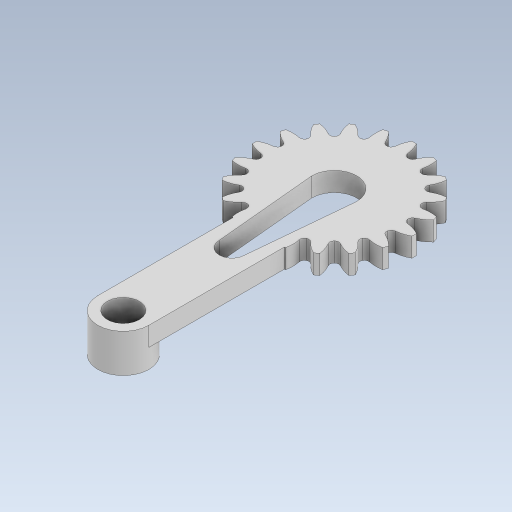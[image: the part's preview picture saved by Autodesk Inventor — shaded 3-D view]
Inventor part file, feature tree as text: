
AUTODESK INVENTOR PART (.ipt)
format: ipt  version: 2023.5 (Build 275446000, 446)  size: 549,888 bytes
history: native  units: in
note: dims shown in document units (in); Inventor stores cm internally (conversion verified against a paired STEP export)
features: extrude x5, sketch x3, fillet x1, pattern_circular x1, plane x1
ambient origin geometry x8: Origin, YZ Plane, XZ Plane, XY Plane, X Axis, Y Axis, Z Axis, Center Point
bodies: Solid1 (feature_tree)
feature tree (11):
  sketch  "Sketch1"  dims[d0=0.7874in d1=0.9843in]
  extrude  "Extrusion1"  Depth=0.9843in
  extrude  "Extrusion3"  Depth=0.0787in
  fillet  "Fillet1"  Radius=0.0276in
  pattern_circular  "Circular Pattern1"  [2 undecoded]
  plane  "Work Plane1"
  sketch  "Sketch2"  dims[d2=0.9055in d3=0.0787in d4=0.0276in]
  extrude  "Extrusion4"  Depth=0.0276in
  extrude  "Extrusion5"  Depth=0.1181in TaperAngle=360.0deg
  extrude  "Extrusion6"  Depth=0.1181in
  sketch  "Sketch3"  dims[d5=0.1181in d6=0.0in d9=0.1181in d10=0.0in d11=0.0276in d12=7.874in d13=360.0deg d15=0.1969in d16=0.315in d17=1.2992in d18=0.2756in d19=0.1969in d20=0.1181in d21=0.0in d22=0.1772in d23=0.0in d24=0.2756in d25=0.1575in d26=0.6299in d27=0.2756in d28=0.1575in d29=0.6299in d30=0.1181in d31=0.0in]
note: 2 required parameter values undecoded (feature->parameter linkage not recoverable at this tier; creation-order binding heuristic only, values carry confidence <= 0.55)
